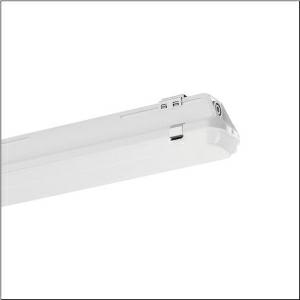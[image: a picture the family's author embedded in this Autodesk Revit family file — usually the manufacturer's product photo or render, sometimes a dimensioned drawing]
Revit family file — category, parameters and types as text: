
# Revit family: monsun_r__21_emergency_51fb10dp487c3h_1d8e
name_source: partatom
category: Lighting Fixtures
units: mm (PartAtom-declared; Revit-internal decimal feet)

## family parameters
Cut with Voids When Loaded = No
Host = Face
Light Source = No
Part Type = Normal
Room Calculation Point = No
Round Connector Dimension = Use Diameter
Shared = No

## types (1)
- --- (1 x LED, 8090 lm, 49.9 W, 4000K)
    Apparent Load = 50 VA
    CIE Flux Codes = 47 77 93 94 100
    Color Rendering = 80
    Color Temperature = 4000K
    Default Elevation = 1800 mm
    Description = Monsun® 21 emergency, damp-proof luminaire, chain hanger, primary optical cover: enclosure, of PMMA, light emission: direct distribution, primary light characteristic: symmetric, installation type: vertical mounting, horizontal mounting, surface-mounted, suspended mounting, LED, rated luminous flux: 8.090lm, luminous efficacy: 176lm/W, light colour: 840, colour temperature: 4000K, control gear: DALI 2, with terminal, 5+3-pole, max. 2.5mm², mains connection: 220..240V, AC, 50/60Hz, rated input power: 50W, control gear: single battery element, battery: LiFePO4, 9Ah, housing, of glass-fibre reinforced polyester, uncoated, bright grey, incl. chain hanger, length: 1.590mm, width: 90mm, height: 88mm, clip for enclosure, of stainless steel (V2A), ceiling mounting element, of stainless steel (V2A), chain hanger, of stainless steel (V2A), protection rating (complete): IP66, insulation class (complete): insulation class I (protective earthing), certification: CE, UKCA, protection symbol: D, impact resistance: IK04, permissible operating ambient temperature: +5..+25°C, standard: EN 50419, EN 60598-2-1, EN 60598-2-22, corresponds to IFS (International Featured Standards) requirements for safety and quality in the food industry, for indoor or canopied outdoor use, no direct snow, no direct sun, no direct rain, LABS conformity tested according to VDMA 24364:2018-05, contact your sales advisor before using the luminaires in applications with unclear chemical exposure, large temperature fluctuations or condensation-forming humidity, packaging unit: 1 piece
    Height = 89 mm
    Lamp = 1 x LED
    Lamp Light Flux = 8090 lm
    Lamp Power = 49.9 W
    Lamp count = 1
    Length = 1590 mm
    Luminous efficacy = 162 lm/W
    Manufacturer = Siteco
    ModVariant = No
    Model = 51FB10DP487C3H
    Mounting Place = Ceiling
    Mounting Type = Surface mounted
    Number of Poles = 1
    OnlyDefault = Yes
    Power Factor = 1
    Product Name = Monsun® 21 emergency
    Product group = damp-proof luminaire
    ProductGroupID = 300
    Protection Class = Protection class I
    Protection Degree = IP 66
    RLX_Detail_Level = 1
    RLX_Emergency_Light_Flux = 0 lm
    RLX_Emergency_Type = 0
    RLX_Emergency_Type_DB = No
    RlxData = <blob elided: 92857 chars, md5=2a574548>
    Socket = socket
    Standby Power = 0 W
    System Light Flux = 8090 lm
    System Power = 50 W
    Type Comments = : luminous flux: 100 % | dim-lin: 254 | 311 mA
    Type Image = l_1319656.jpg
    URL = http://relux.com
    VarID = @adj_031590
    Voltage = 0 V
    Weight = 0.00 kg
    Width = 90 mm

## geometry (parser evidence)
native form markers: Blend x4, Sweep x14
no freeform markers — native parametric forms only
